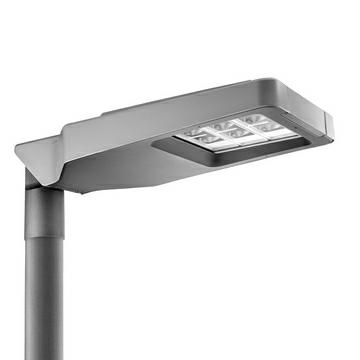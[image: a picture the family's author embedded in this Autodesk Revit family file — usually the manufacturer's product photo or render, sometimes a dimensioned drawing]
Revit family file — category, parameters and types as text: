
# Revit family: Lighting-StreetLighting-GEWISS-ROAD[5]MINI-LED_OPTIC_WIDE_CLI
name_source: partatom
category: Apparecchi per illuminazione
units: mm (PartAtom-declared; Revit-internal decimal feet)

## family parameters
Basato su piano di lavoro = No
Condiviso = No
Punto di calcolo locali = No
Quota connettore circolare = Usa diametro
Sempre verticale = Sì
Sorgente d'illuminazione = No
Taglio con vuoti quando caricato = No
Tipo di parte = Normale

## types (28) — shared parameters
Applicazione = External
Carico apparente = 53 VA
Catalogue = LIGHTING
Commenti sul wattaggio = 53W
IDF = 85536a03-eff7-45b7-82af-033095416c36
IDT = 022a80ee4c80461ea9288278e8deede6
IP degree = IP66
Immagine tipo = GWR5276M.jpg
Insulation class = I
Produttore = GEWISS S.p.A.
SEO = Street lighting
Shock resistance = IK08
Technical sheet = https://www.gewiss.com
URL = https://www.gewiss.com
Version file RFA = 20.11
Warranty = 5 years

## per-type parameters (varying)
- GWR5772 - ROAD 5 MINI S.AL.2M 4000K 700mA O.W CL.I: Catalogue Range=ROAD [5]; Colour temperature=4000 K (CRI 70); Colour temperature:=4000 K (CRI 70); Descrizione=ROAD 5 MINI S.AL.2M 4000K 700mA O.W CL.I; EAN code=8011564873339; Electrocod=244C; LED LifeTime (L80B05)=77000H; LED current.=0,7A; Lamp-=LED; Lumen output (lm)=5240; Maximum surface exposed to the wind=0,15M2; Minimum distance from the illuminated object=1M; Modello=GWR5772; No. Chorus modules=2 (2x3 LED); Nominal flux (lm)=6240; Number of modules=2 (2x3 LED); Operating temperature:=-25 +50 °C; Optic=W - ULOR: 0%; Overvoltage resistance=12 KV (Common and dfferential mode); Pilot current=0,7A; System power=53W; Tilt adjustable=-20° ÷ +10° side bracket - -10° ÷ +20° pole head; Tipo alimentatore=Constant Current Driver Led; Tipologia=Stand alone; Type of lamp=LED; Voltage-=220/240 V - 50/60 Hz - Stand alone; Weight (kg)=6,6; Weight (kg):=6,6; Working temperature=-25 +50 °C
- GWR5771B30K - ROAD5 MINI WIDE 1M 3000K 0,7A CL1 BIREG: Body=Die-cast aluminium -; Catalogue Range=ROAD [5]; Classification:=-; Color Rendering Index=CRI-70; Colore=Graphite grey; Colour :=Powder coating; Colour temperature=3000K; Colour temperature:=3000 K (CRI>80); Context=Street and parking lighting; Control System=Bi-power with self-learning; DIN 18032-3 certification=-; Descrizione=GWR5771B30K - ROAD5 MINI WIDE 1M 3000K 0,7A CL1 BIREG; Device with reduced surface temperature=-; Driver=Included; Driver Box=Built-in; Efficiency (lm/W)=100; Electrocod=244C; Eletrical and lighting features=-; External screw=Stainless steel; Fixing=Pole Head - Outreach; Gasket=Anti-aging silicone; General information=-; Glow Wire Test :=-; IPEA=ROAD = A ++ // LARGE AREAS = A3 + // CYCLOPEDONALS = A ++ // GREEN AREAS = A ++ // HISTORICAL CENTER = A5 +; Installationa and maintenance=-; LED Life Time (L80B05)=77000H; LED Maintenance=Not available; LED current.=0,7A; Lamp-=LED; Lifetime=L90B10 (Tq+25°C) = 100.000 h - L90B10 (Tq+50°C) = 75.000 h; Locking Hook=Integrated front handle; Lumen output (lm)=2800; Luminaire=LED Road Equipment; Materials=-; Maximum surface exposed to the wind=0,149999999999999M2; Maximum surface exposed to the wind :=0.15 m²; Minimum distance from the illuminated object=1M; Modello=GWR5771B30K; Mouting and installation=Pole Head - Outreach; Nominal flux (lm)=2700; Number of modules=1 (1x3 LED); Operating temperature :=-25 +50 °C; Operating temperature:=-25 +50 °C; Optic=WIDE; Optic :=Metallized polycarbonate reflector; Optic Maintenance=Not available; Optic and illuminating features=-; Overvoltage protection=DM 10KV / CM 10KV; Overvoltage resistance :=Common and dfferential mode: 10KV; Photobiological Risk Class=RG0; Power supply operation=Bi power; Rated frequency (Hz)=50 / 60; Shield type=4mm thick flat tempered glass; Standard Deviation Colour Matching=SDCM = 5; Standard-=EN 60598-2-3, EN 60598-1 IEC/TR 62778; Standards and approvals=-; Stocking temperature=-; Supply voltage=220 - 240 V; System power=28W; System power :=28 W @ 0.7A; Tilt adjustable=-20° ÷ +10° side bracket - -10° ÷ +20° pole head; Tilt-=-20° ÷ +10° side bracket - -10° ÷ +20° pole head; Tipo alimentatore=Constant Current Driver Led; Tipologia=Bi power; Type of light source=LED - Not replaceable; Unified Glare Rating=G*3 - ULOR = 0; Unique digital code (Datamatrix)=Currently not present; Voltage-=220/240 V - 50/60 Hz - Bi-power with self-learning; Weight (kg):=6,4; Wiring=Isolating switch
- GWR571230K - ROAD5 MINI WIDE 2M 3000K 1,0A CL1: Body=Die-cast aluminium -; Catalogue Range=ROAD [5]; Classification:=-; Color Rendering Index=CRI-70; Colore=Graphite grey; Colour :=Powder coating; Colour temperature=3000K; Colour temperature:=3000 K (CRI>80); Context=Street and parking lighting; Control System=Stand alone; DIN 18032-3 certification=-; Descrizione=GWR571230K - ROAD5 MINI WIDE 2M 3000K 1,0A CL1; Device with reduced surface temperature=-; Driver=Included; Driver Box=Built-in; Efficiency (lm/W)=101; Electrocod=244C; Eletrical and lighting features=-; External screw=Stainless steel; Fixing=Pole Head - Outreach; Gasket=Anti-aging silicone; General information=-; Glow Wire Test :=-; IPEA=ROAD = A ++ // LARGE AREAS = A3 + // CYCLOPEDONALS = A + // GREEN AREAS = A + // HISTORICAL CENTER = A5 +; Installationa and maintenance=-; LED Life Time (L80B05)=120000H; LED Maintenance=Not available; LED current.=0,9A; Lamp-=LED; Lifetime=L90B10 (Tq+25°C) = 100.000 h - L90B10 (Tq+40°C) = 75.000 h; Locking Hook=Integrated front handle; Lumen output (lm)=6800; Luminaire=LED Road Equipment; Materials=-; Maximum surface exposed to the wind=0,149999999999999M2; Maximum surface exposed to the wind :=0.15 m²; Minimum distance from the illuminated object=1M; Modello=GWR571230K; Mouting and installation=Pole Head - Outreach; Nominal flux (lm)=8280; Number of modules=2 (2x3 LED); Operating temperature :=-25 +40 °C; Operating temperature:=-25 +40 °C; Optic=WIDE; Optic :=Metallized polycarbonate reflector; Optic Maintenance=Not available; Optic and illuminating features=-; Overvoltage protection=DM 10KV / CM 10KV; Overvoltage resistance :=Common and dfferential mode: 10KV; Photobiological Risk Class=RG0; Rated frequency (Hz)=50 / 60; Shield type=4mm thick flat tempered glass; Standard Deviation Colour Matching=SDCM = 5; Standard-=EN 60598-2-3, EN 60598-1 IEC/TR 62778; Standards and approvals=-; Stocking temperature=-; Supply voltage=220 - 240 V; System power=76W; System power :=67 W @ 0.9A; Tilt adjustable=-20° ÷ +10° side bracket - -10° ÷ +20° pole head; Tilt-=-20° ÷ +10° side bracket - -10° ÷ +20° pole head; Tipo alimentatore=Constant Current Driver Led; Tipologia=Stand alone; Type of light source=LED - Not replaceable; Unified Glare Rating=G*3 - ULOR = 0; Unique digital code (Datamatrix)=Currently not present; Voltage-=220/240 V - 50/60 Hz - Stand alone; Weight (kg):=6,6; Wiring=Isolating switch
- GWR571130K - ROAD5 MINI WIDE 1M 3000K 1,0A CL1: Body=Die-cast aluminium -; Catalogue Range=ROAD [5]; Classification:=-; Color Rendering Index=CRI-70; Colore=Graphite grey; Colour :=Powder coating; Colour temperature=3000K; Colour temperature:=3000 K (CRI>80); Context=Street and parking lighting; Control System=Stand alone; DIN 18032-3 certification=-; Descrizione=GWR571130K - ROAD5 MINI WIDE 1M 3000K 1,0A CL1; Device with reduced surface temperature=-; Driver=Included; Driver Box=Built-in; Efficiency (lm/W)=97; Electrocod=244C; Eletrical and lighting features=-; External screw=Stainless steel; Fixing=Pole Head - Outreach; Gasket=Anti-aging silicone; General information=-; Glow Wire Test :=-; IPEA=ROAD = A ++ // LARGE AREAS = A ++ // CYCLOPEDONALS = A + // GREEN AREAS = A + // HISTORICAL CENTER = A5 +; Installationa and maintenance=-; LED Life Time (L80B05)=120000H; LED Maintenance=Not available; LED current.=1A; Lamp-=LED; Lifetime=L90B10 (Tq+25°C) = 100.000 h - L90B10 (Tq+40°C) = 75.000 h; Locking Hook=Integrated front handle; Lumen output (lm)=3700; Luminaire=LED Road Equipment; Materials=-; Maximum surface exposed to the wind=0,149999999999999M2; Maximum surface exposed to the wind :=0.15 m²; Minimum distance from the illuminated object=1M; Modello=GWR571130K; Mouting and installation=Pole Head - Outreach; Nominal flux (lm)=4140; Number of modules=1 (1x3 LED); Operating temperature :=-25 +40 °C; Operating temperature:=-25 +40 °C; Optic=WIDE; Optic :=Metallized polycarbonate reflector; Optic Maintenance=Not available; Optic and illuminating features=-; Overvoltage protection=DM 10KV / CM 10KV; Overvoltage resistance :=Common and dfferential mode: 10KV; Photobiological Risk Class=RG0; Rated frequency (Hz)=50 / 60; Shield type=4mm thick flat tempered glass; Standard Deviation Colour Matching=SDCM = 5; Standard-=EN 60598-2-3, EN 60598-1 IEC/TR 62778; Standards and approvals=-; Stocking temperature=-; Supply voltage=220 - 240 V; System power=38W; System power :=38 W @ 1A; Tilt adjustable=-20° ÷ +10° side bracket - -10° ÷ +20° pole head; Tilt-=-20° ÷ +10° side bracket - -10° ÷ +20° pole head; Tipo alimentatore=Constant Current Driver Led; Tipologia=Stand alone; Type of light source=LED - Not replaceable; Unified Glare Rating=G*3 - ULOR = 0; Unique digital code (Datamatrix)=Currently not present; Voltage-=220/240 V - 50/60 Hz - Stand alone; Weight (kg):=6,4; Wiring=Isolating switch
- GWR5772M30K - ROAD5 MINI WIDE 2M 3000K 0,7A CL1 1-10V: Body=Die-cast aluminium -; Catalogue Range=ROAD [5]; Classification:=-; Color Rendering Index=CRI-70; Colore=Graphite grey; Colour :=Powder coating; Colour temperature=3000K; Colour temperature:=3000 K (CRI>80); Context=Street and parking lighting; Control System=Dimmable 1-10 V; DIN 18032-3 certification=-; Descrizione=GWR5772M30K - ROAD5 MINI WIDE 2M 3000K 0,7A CL1 1-10V; Device with reduced surface temperature=-; Driver=Included; Driver Box=Built-in; Efficiency (lm/W)=102; Electrocod=244C; Eletrical and lighting features=-; External screw=Stainless steel; Fixing=Pole Head - Outreach; Gasket=Anti-aging silicone; General information=-; Glow Wire Test :=-; IPEA=ROAD = A ++ // LARGE AREAS = A3 + // CYCLOPEDONALS = A ++ // GREEN AREAS = A ++ // HISTORICAL CENTER = A5 +; Installationa and maintenance=-; LED Life Time (L80B05)=77000H; LED Maintenance=Not available; LED current.=0,7A; Lamp-=LED; Lifetime=L90B10 (Tq+25°C) = 100.000 h - L90B10 (Tq+50°C) = 75.000 h; Locking Hook=Integrated front handle; Lumen output (lm)=5500; Luminaire=LED Road Equipment; Materials=-; Maximum surface exposed to the wind=0,149999999999999M2; Maximum surface exposed to the wind :=0.15 m²; Minimum distance from the illuminated object=1M; Modello=GWR5772M30K; Mouting and installation=Pole Head - Outreach; Nominal flux (lm)=5400; Number of modules=2 (2x3 LED); Operating temperature :=-25 +50 °C; Operating temperature:=-25 +50 °C; Optic=WIDE; Optic :=Metallized polycarbonate reflector; Optic Maintenance=Not available; Optic and illuminating features=-; Overvoltage protection=DM 10KV / CM 10KV; Overvoltage resistance :=Common and dfferential mode: 10KV; Photobiological Risk Class=RG0; Power supply operation=Dimmable; Rated frequency (Hz)=50 / 60; Shield type=4mm thick flat tempered glass; Standard Deviation Colour Matching=SDCM = 5; Standard-=EN 60598-2-3, EN 60598-1 IEC/TR 62778; Standards and approvals=-; Stocking temperature=-; Supply voltage=220 - 240 V; System power=53W; System power :=54 W @ 0.7A; Tilt adjustable=-20° ÷ +10° side bracket - -10° ÷ +20° pole head; Tilt-=-20° ÷ +10° side bracket - -10° ÷ +20° pole head; Tipo alimentatore=Constant Current Driver Led; Tipologia=Dimmable; Type of light source=LED - Not replaceable; Unified Glare Rating=G*3 - ULOR = 0; Unique digital code (Datamatrix)=Currently not present; Voltage-=220/240 V - 50/60 Hz - Dimmable 1-10 V; Weight (kg):=6,6; Wiring=Isolating switch
- GWR5712B - ROAD5 MINI WIDE 2M 4000K 1,0A CL1 BIREG: Catalogue Range=ROAD [5]; Colour temperature=4000 K (CRI 70); Colour temperature:=4000 K (CRI 70); Descrizione=ROAD 5 MINI BI-POW.2M 4000K 1A O.W CL.I; EAN code=8011564873056; Electrocod=244C; LED LifeTime (L80B05)=120000H; LED current.=1A; Lamp-=LED; Lumen output (lm)=7680; Maximum surface exposed to the wind=0,15M2; Minimum distance from the illuminated object=1M; Modello=GWR5712B; No. Chorus modules=2 (2x3 LED); Nominal flux (lm)=9540; Number of modules=2 (2x3 LED); Operating temperature:=-25 +40 °C; Optic=W - ULOR: 0%; Overvoltage resistance=12 KV (Common and dfferential mode); Pilot current=1A; Power supply operation=Bi power; System power=77W; Tilt adjustable=-20° ÷ +10° side bracket - -10° ÷ +20° pole head; Tipo alimentatore=Constant Current Driver Led; Tipologia=Bi power; Type of lamp=LED; Voltage-=220/240 V - 50/60 Hz - Bi-power with self-learning; Weight (kg)=6,6; Weight (kg):=6,6; Working temperature=-25 +40 °C
- GWR5712 - ROAD 5 MINI S.AL.2M 4000K 1A O.W CL.I: Catalogue Range=ROAD [5]; Colour temperature=4000 K (CRI 70); Colour temperature:=4000 K (CRI 70); Descrizione=ROAD 5 MINI S.AL.2M 4000K 1A O.W CL.I; EAN code=8011564873049; Electrocod=244C; LED LifeTime (L80B05)=120000H; LED current.=1A; Lamp-=LED; Lumen output (lm)=7680; Maximum surface exposed to the wind=0,15M2; Minimum distance from the illuminated object=1M; Modello=GWR5712; No. Chorus modules=2 (2x3 LED); Nominal flux (lm)=9540; Number of modules=2 (2x3 LED); Operating temperature:=-25 +40 °C; Optic=W - ULOR: 0%; Overvoltage resistance=12 KV (Common and dfferential mode); Pilot current=1A; System power=76W; Tilt adjustable=-20° ÷ +10° side bracket - -10° ÷ +20° pole head; Tipo alimentatore=Constant Current Driver Led; Tipologia=Stand alone; Type of lamp=LED; Voltage-=220/240 V - 50/60 Hz - Stand alone; Weight (kg)=6,6; Weight (kg):=6,6; Working temperature=-25 +40 °C
- GWR5711 - ROAD 5 MINI S.AL.1M 4000K 1A O.W CL.I: Catalogue Range=ROAD [5]; Colour temperature=4000 K (CRI 70); Colour temperature:=4000 K (CRI 70); Descrizione=ROAD 5 MINI S.AL.1M 4000K 1A O.W CL.I; EAN code=8011564873018; Electrocod=244C; LED LifeTime (L80B05)=120000H; LED current.=1A; Lamp-=LED; Lumen output (lm)=3840; Maximum surface exposed to the wind=0,15M2; Minimum distance from the illuminated object=1M; Modello=GWR5711; No. Chorus modules=1 (1x3 LED); Nominal flux (lm)=4770; Number of modules=1 (1x3 LED); Operating temperature:=-25 +40 °C; Optic=W - ULOR: 0%; Overvoltage resistance=12 KV (Common and dfferential mode); Pilot current=1A; System power=38W; Tilt adjustable=-20° ÷ +10° side bracket - -10° ÷ +20° pole head; Tipo alimentatore=Constant Current Driver Led; Tipologia=Stand alone; Type of lamp=LED; Voltage-=220/240 V - 50/60 Hz - Stand alone; Weight (kg)=6,4; Weight (kg):=6,4; Working temperature=-25 +40 °C
- GWR5711V - ROAD5 MINI V.WIDE 1M 4000K 1,0A CL1: Body=Die-cast aluminium -; Classification:=-; Color Rendering Index=CRI-70; Colore=Graphite grey; Colour :=Powder coating; Colour temperature=4000K; Context=Street and parking lighting; Control System=DALI; DIN 18032-3 certification=-; Descrizione=GWR5711V - ROAD5 MINI V.WIDE 1M 4000K 1,0A CL1; Device with reduced surface temperature=-; Driver=Included; Driver Box=Built-in; Efficiency (lm/W)=110; Eletrical and lighting features=-; External screw=Stainless steel; Fixing=Pole Head - Outreach; Gasket=Anti-aging silicone; General information=-; Glow Wire Test :=-; IPEA=ROAD = A4 + // LARGE AREAS = A4 + // CYCLOPEDONALS = A3 + // GREEN AREAS = A3 + // HISTORICAL CENTER = A6 +; Installationa and maintenance=-; LED Maintenance=Not available; Lifetime=L90B10 (Tq+25°C) = 100.000 h - L90B10 (Tq+40°C) = 75.000 h; Locking Hook=Integrated front handle; Lumen output (lm)=4300; Luminaire=LED Road Equipment; Materials=-; Maximum surface exposed to the wind :=0.15 m²; Modello=GWR5711V; Mouting and installation=Pole Head - Outreach; Number of modules=1 (1x3 LED); Operating temperature :=-25 +40 °C; Optic=WIDE; Optic :=Metallized polycarbonate reflector; Optic Maintenance=Not available; Optic and illuminating features=-; Overvoltage protection=DM 10KV / CM 10KV; Photobiological Risk Class=RG0; Rated frequency (Hz)=50 / 60; Shield type=4mm thick flat tempered glass; Standard Deviation Colour Matching=SDCM = 5; Standard-=EN 60598-2-3, EN 60598-1 IEC/TR 62778; Standards and approvals=-; Stocking temperature=-; Supply voltage=220 - 240 V; System power :=39 W @ 1A; Tilt-=-20° ÷ +10° side bracket - -10° ÷ +20° pole head; Type of light source=LED - Not replaceable; Unified Glare Rating=G*3 - ULOR = 0; Unique digital code (Datamatrix)=Currently not present; Weight (kg):=6,4; Wiring=Isolating switch
- GWR5772B30K - ROAD5 MINI WIDE 2M 3000K 0,7A CL1 BIREG: Body=Die-cast aluminium -; Catalogue Range=ROAD [5]; Classification:=-; Color Rendering Index=CRI-70; Colore=Graphite grey; Colour :=Powder coating; Colour temperature=3000K; Colour temperature:=3000 K (CRI>80); Context=Street and parking lighting; Control System=Bi-power with self-learning; DIN 18032-3 certification=-; Descrizione=GWR5772B30K - ROAD5 MINI WIDE 2M 3000K 0,7A CL1 BIREG; Device with reduced surface temperature=-; Driver=Included; Driver Box=Built-in; Efficiency (lm/W)=102; Electrocod=244C; Eletrical and lighting features=-; External screw=Stainless steel; Fixing=Pole Head - Outreach; Gasket=Anti-aging silicone; General information=-; Glow Wire Test :=-; IPEA=ROAD = A ++ // LARGE AREAS = A3 + // CYCLOPEDONALS = A ++ // GREEN AREAS = A ++ // HISTORICAL CENTER = A5 +; Installationa and maintenance=-; LED Life Time (L80B05)=77000H; LED Maintenance=Not available; LED current.=0,7A; Lamp-=LED; Lifetime=L90B10 (Tq+25°C) = 100.000 h - L90B10 (Tq+50°C) = 75.000 h; Locking Hook=Integrated front handle; Lumen output (lm)=5500; Luminaire=LED Road Equipment; Materials=-; Maximum surface exposed to the wind=0,149999999999999M2; Maximum surface exposed to the wind :=0.15 m²; Minimum distance from the illuminated object=1M; Modello=GWR5772B30K; Mouting and installation=Pole Head - Outreach; Nominal flux (lm)=5400; Number of modules=2 (2x3 LED); Operating temperature :=-25 +50 °C; Operating temperature:=-25 +50 °C; Optic=WIDE; Optic :=Metallized polycarbonate reflector; Optic Maintenance=Not available; Optic and illuminating features=-; Overvoltage protection=DM 10KV / CM 10KV; Overvoltage resistance :=Common and dfferential mode: 10KV; Photobiological Risk Class=RG0; Power supply operation=Bi power; Rated frequency (Hz)=50 / 60; Shield type=4mm thick flat tempered glass; Standard Deviation Colour Matching=SDCM = 5; Standard-=EN 60598-2-3, EN 60598-1 IEC/TR 62778; Standards and approvals=-; Stocking temperature=-; Supply voltage=220 - 240 V; System power=54W; System power :=54 W @ 0.7A; Tilt adjustable=-20° ÷ +10° side bracket - -10° ÷ +20° pole head; Tilt-=-20° ÷ +10° side bracket - -10° ÷ +20° pole head; Tipo alimentatore=Constant Current Driver Led; Tipologia=Bi power; Type of light source=LED - Not replaceable; Unified Glare Rating=G*3 - ULOR = 0; Unique digital code (Datamatrix)=Currently not present; Voltage-=220/240 V - 50/60 Hz - Bi-power with self-learning; Weight (kg):=6,6; Wiring=Isolating switch
- GWR577130K - ROAD5 MINI WIDE 1M 3000K 0,7A CL1: Body=Die-cast aluminium -; Catalogue Range=ROAD [5]; Classification:=-; Color Rendering Index=CRI-70; Colore=Graphite grey; Colour :=Powder coating; Colour temperature=3000K; Colour temperature:=3000 K (CRI>80); Context=Street and parking lighting; Control System=Stand alone; DIN 18032-3 certification=-; Descrizione=GWR577130K - ROAD5 MINI WIDE 1M 3000K 0,7A CL1; Device with reduced surface temperature=-; Driver=Included; Driver Box=Built-in; Efficiency (lm/W)=104; Electrocod=244C; Eletrical and lighting features=-; External screw=Stainless steel; Fixing=Pole Head - Outreach; Gasket=Anti-aging silicone; General information=-; Glow Wire Test :=-; IPEA=ROAD = A3 + // LARGE AREAS = A3 + // CYCLOPEDONALS = A ++ // GREEN AREAS = A ++ // HISTORICAL CENTER = A6 +; Installationa and maintenance=-; LED Life Time (L80B05)=77000H; LED Maintenance=Not available; LED current.=0,7A; Lamp-=LED; Lifetime=L90B10 (Tq+25°C) = 100.000 h - L90B10 (Tq+50°C) = 75.000 h; Locking Hook=Integrated front handle; Lumen output (lm)=2800; Luminaire=LED Road Equipment; Materials=-; Maximum surface exposed to the wind=0,149999999999999M2; Maximum surface exposed to the wind :=0.15 m²; Minimum distance from the illuminated object=1M; Modello=GWR577130K; Mouting and installation=Pole Head - Outreach; Nominal flux (lm)=2700; Number of modules=1 (1x3 LED); Operating temperature :=-25 +50 °C; Operating temperature:=-25 +50 °C; Optic=WIDE; Optic :=Metallized polycarbonate reflector; Optic Maintenance=Not available; Optic and illuminating features=-; Overvoltage protection=DM 10KV / CM 10KV; Overvoltage resistance :=Common and dfferential mode: 10KV; Photobiological Risk Class=RG0; Rated frequency (Hz)=50 / 60; Shield type=4mm thick flat tempered glass; Standard Deviation Colour Matching=SDCM = 5; Standard-=EN 60598-2-3, EN 60598-1 IEC/TR 62778; Standards and approvals=-; Stocking temperature=-; Supply voltage=220 - 240 V; System power=27W; System power :=27 W @ 0.7A; Tilt adjustable=-20° ÷ +10° side bracket - -10° ÷ +20° pole head; Tilt-=-20° ÷ +10° side bracket - -10° ÷ +20° pole head; Tipo alimentatore=Constant Current Driver Led; Tipologia=Stand alone; Type of light source=LED - Not replaceable; Unified Glare Rating=G*3 - ULOR = 0; Unique digital code (Datamatrix)=Currently not present; Voltage-=220/240 V - 50/60 Hz - Stand alone; Weight (kg):=6,4; Wiring=Isolating switch
- GWR5711B - ROAD5 MINI WIDE 1M 4000K 1,0A CL1 BIREG: Catalogue Range=ROAD [5]; Colour temperature=4000 K (CRI 70); Colour temperature:=4000 K (CRI 70); Descrizione=ROAD 5 MINI BI-POW.1M 4000K 1A O.W CL.I; EAN code=8011564873025; Electrocod=244C; LED LifeTime (L80B05)=120000H; LED current.=1A; Lamp-=LED; Lumen output (lm)=3840; Maximum surface exposed to the wind=0,15M2; Minimum distance from the illuminated object=1M; Modello=GWR5711B; No. Chorus modules=1 (1x3 LED); Nominal flux (lm)=4770; Number of modules=1 (1x3 LED); Operating temperature:=-25 +40 °C; Optic=W - ULOR: 0%; Overvoltage resistance=12 KV (Common and dfferential mode); Pilot current=1A; Power supply operation=Bi power; System power=39W; Tilt adjustable=-20° ÷ +10° side bracket - -10° ÷ +20° pole head; Tipo alimentatore=Constant Current Driver Led; Tipologia=Bi power; Type of lamp=LED; Voltage-=220/240 V - 50/60 Hz - Bi-power with self-learning; Weight (kg)=6,4; Weight (kg):=6,4; Working temperature=-25 +40 °C
- GWR5731 - ROAD5 MINI WIDE 1M 4000K 0,35A CL1: Catalogue Range=ROAD [5]; Colour temperature=4000 K (CRI 70); Colour temperature:=4000 K (CRI 70); Descrizione=ROAD 5 MINI S.AL.1M 4000K 350mA O.W CL.I; EAN code=8011564873193; Electrocod=244C; LED LifeTime (L80B05)=77000H; LED current.=0,35A; Lamp-=LED; Lumen output (lm)=1310; Maximum surface exposed to the wind=0,15M2; Minimum distance from the illuminated object=1M; Modello=GWR5731; No. Chorus modules=1 (1x3 LED); Nominal flux (lm)=1560; Number of modules=1 (1x3 LED); Operating temperature:=-25 +50 °C; Optic=W - ULOR: 0%; Overvoltage resistance=12 KV (Common and dfferential mode); Pilot current=0,35A; System power=14W; Tilt adjustable=-20° ÷ +10° side bracket - -10° ÷ +20° pole head; Tipo alimentatore=Constant Current Driver Led; Tipologia=Stand alone; Type of lamp=LED; Voltage-=220/240 V - 50/60 Hz - Stand alone; Weight (kg)=6,4; Weight (kg):=6,4; Working temperature=-25 +50 °C
- GWR5771M30K - ROAD5 MINI WIDE 1M 3000K 0,7A CL1 1-10V: Body=Die-cast aluminium -; Catalogue Range=ROAD [5]; Classification:=-; Color Rendering Index=CRI-70; Colore=Graphite grey; Colour :=Powder coating; Colour temperature=3000K; Colour temperature:=3000 K (CRI>80); Context=Street and parking lighting; Control System=Dimmable 1-10 V; DIN 18032-3 certification=-; Descrizione=GWR5771M30K - ROAD5 MINI WIDE 1M 3000K 0,7A CL1 1-10V; Device with reduced surface temperature=-; Driver=Included; Driver Box=Built-in; Efficiency (lm/W)=100; Electrocod=244C; Eletrical and lighting features=-; External screw=Stainless steel; Fixing=Pole Head - Outreach; Gasket=Anti-aging silicone; General information=-; Glow Wire Test :=-; IPEA=ROAD = A ++ // LARGE AREAS = A3 + // CYCLOPEDONALS = A ++ // GREEN AREAS = A ++ // HISTORICAL CENTER = A5 +; Installationa and maintenance=-; LED Life Time (L80B05)=77000H; LED Maintenance=Not available; LED current.=0,7A; Lamp-=LED; Lifetime=L90B10 (Tq+25°C) = 100.000 h - L90B10 (Tq+50°C) = 75.000 h; Locking Hook=Integrated front handle; Lumen output (lm)=2800; Luminaire=LED Road Equipment; Materials=-; Maximum surface exposed to the wind=0,149999999999999M2; Maximum surface exposed to the wind :=0.15 m²; Minimum distance from the illuminated object=1M; Modello=GWR5771M30K; Mouting and installation=Pole Head - Outreach; Nominal flux (lm)=2700; Number of modules=1 (1x3 LED); Operating temperature :=-25 +50 °C; Operating temperature:=-25 +50 °C; Optic=WIDE; Optic :=Metallized polycarbonate reflector; Optic Maintenance=Not available; Optic and illuminating features=-; Overvoltage protection=DM 10KV / CM 10KV; Overvoltage resistance :=Common and dfferential mode: 10KV; Photobiological Risk Class=RG0; Power supply operation=Dimmable; Rated frequency (Hz)=50 / 60; Shield type=4mm thick flat tempered glass; Standard Deviation Colour Matching=SDCM = 5; Standard-=EN 60598-2-3, EN 60598-1 IEC/TR 62778; Standards and approvals=-; Stocking temperature=-; Supply voltage=220 - 240 V; System power=27W; System power :=28 W @ 0.7A; Tilt adjustable=-20° ÷ +10° side bracket - -10° ÷ +20° pole head; Tilt-=-20° ÷ +10° side bracket - -10° ÷ +20° pole head; Tipo alimentatore=Constant Current Driver Led; Tipologia=Dimmable; Type of light source=LED - Not replaceable; Unified Glare Rating=G*3 - ULOR = 0; Unique digital code (Datamatrix)=Currently not present; Voltage-=220/240 V - 50/60 Hz - Dimmable 1-10 V; Weight (kg):=6,4; Wiring=Isolating switch
- GWR5711M - ROAD5 MINI WIDE 1M 4000K 1,0A CL1 1-10V: Catalogue Range=ROAD [5]; Colour temperature=4000 K (CRI 70); Colour temperature:=4000 K (CRI 70); Descrizione=ROAD 5 MINI DIM.1M 4000K 1A O.W CL.I; EAN code=8011564873032; Electrocod=244C; LED LifeTime (L80B05)=120000H; LED current.=1A; Lamp-=LED; Lumen output (lm)=3840; Maximum surface exposed to the wind=0,15M2; Minimum distance from the illuminated object=1M; Modello=GWR5711M; No. Chorus modules=1 (1x3 LED); Nominal flux (lm)=4770; Number of modules=1 (1x3 LED); Operating temperature:=-25 +40 °C; Optic=W - ULOR: 0%; Overvoltage resistance=12 KV (Common and dfferential mode); Pilot current=1A; Power supply operation=Dimmable; System power=38W; Tilt adjustable=-20° ÷ +10° side bracket - -10° ÷ +20° pole head; Tipo alimentatore=Constant Current Driver Led; Tipologia=Dimmable; Type of lamp=LED; Voltage-=220/240 V - 50/60 Hz - Dimmable 1-10 V; Weight (kg)=6,4; Weight (kg):=6,4; Working temperature=-25 +40 °C
- GWR5712M - ROAD5 MINI WIDE 2M 4000K 1,0A CL1 1-10V: Catalogue Range=ROAD [5]; Colour temperature=4000 K (CRI 70); Colour temperature:=4000 K (CRI 70); Descrizione=ROAD 5 MINI DIM.2M 4000K 1A O.W CL.I; EAN code=8011564873063; Electrocod=244C; LED LifeTime (L80B05)=120000H; LED current.=1A; Lamp-=LED; Lumen output (lm)=7680; Maximum surface exposed to the wind=0,15M2; Minimum distance from the illuminated object=1M; Modello=GWR5712M; No. Chorus modules=2 (2x3 LED); Nominal flux (lm)=9540; Number of modules=2 (2x3 LED); Operating temperature:=-25 +40 °C; Optic=W - ULOR: 0%; Overvoltage resistance=12 KV (Common and dfferential mode); Pilot current=1A; Power supply operation=Dimmable; System power=76W; Tilt adjustable=-20° ÷ +10° side bracket - -10° ÷ +20° pole head; Tipo alimentatore=Constant Current Driver Led; Tipologia=Dimmable; Type of lamp=LED; Voltage-=220/240 V - 50/60 Hz - Dimmable 1-10 V; Weight (kg)=6,6; Weight (kg):=6,6; Working temperature=-25 +40 °C
- GWR5712M30K - ROAD5 MINI WIDE 2M 3000K 1,0A CL1 1-10V: Body=Die-cast aluminium -; Catalogue Range=ROAD [5]; Classification:=-; Color Rendering Index=CRI-70; Colore=Graphite grey; Colour :=Powder coating; Colour temperature=3000K; Colour temperature:=3000 K (CRI>80); Context=Street and parking lighting; Control System=Dimmable 1-10 V; DIN 18032-3 certification=-; Descrizione=GWR5712M30K - ROAD5 MINI WIDE 2M 3000K 1,0A CL1 1-10V; Device with reduced surface temperature=-; Driver=Included; Driver Box=Built-in; Efficiency (lm/W)=96; Electrocod=244C; Eletrical and lighting features=-; External screw=Stainless steel; Fixing=Pole Head - Outreach; Gasket=Anti-aging silicone; General information=-; Glow Wire Test :=-; IPEA=ROAD = A + // LARGE AREAS = A ++ // CYCLOPEDONALS = A + // GREEN AREAS = A + // HISTORICAL CENTER = A5 +; Installationa and maintenance=-; LED Life Time (L80B05)=120000H; LED Maintenance=Not available; LED current.=1A; Lamp-=LED; Lifetime=L90B10 (Tq+25°C) = 100.000 h - L90B10 (Tq+40°C) = 75.000 h; Locking Hook=Integrated front handle; Lumen output (lm)=7400; Luminaire=LED Road Equipment; Materials=-; Maximum surface exposed to the wind=0,149999999999999M2; Maximum surface exposed to the wind :=0.15 m²; Minimum distance from the illuminated object=1M; Modello=GWR5712M30K; Mouting and installation=Pole Head - Outreach; Nominal flux (lm)=8280; Number of modules=2 (2x3 LED); Operating temperature :=-25 +40 °C; Operating temperature:=-25 +40 °C; Optic=WIDE; Optic :=Metallized polycarbonate reflector; Optic Maintenance=Not available; Optic and illuminating features=-; Overvoltage protection=DM 10KV / CM 10KV; Overvoltage resistance :=Common and dfferential mode: 10KV; Photobiological Risk Class=RG0; Power supply operation=Dimmable; Rated frequency (Hz)=50 / 60; Shield type=4mm thick flat tempered glass; Standard Deviation Colour Matching=SDCM = 5; Standard-=EN 60598-2-3, EN 60598-1 IEC/TR 62778; Standards and approvals=-; Stocking temperature=-; Supply voltage=220 - 240 V; System power=76W; System power :=77 W @ 1A; Tilt adjustable=-20° ÷ +10° side bracket - -10° ÷ +20° pole head; Tilt-=-20° ÷ +10° side bracket - -10° ÷ +20° pole head; Tipo alimentatore=Constant Current Driver Led; Tipologia=Dimmable; Type of light source=LED - Not replaceable; Unified Glare Rating=G*3 - ULOR = 0; Unique digital code (Datamatrix)=Currently not present; Voltage-=220/240 V - 50/60 Hz - Dimmable 1-10 V; Weight (kg):=6,6; Wiring=Isolating switch
- GWR5772M - ROAD5 MINI WIDE 2M 4000K 0,7A CL1 1-10V: Catalogue Range=ROAD [5]; Colour temperature=4000 K (CRI 70); Colour temperature:=4000 K (CRI 70); Descrizione=ROAD 5 MINI DIM.2M 4000K 700mA O.W CL.I; EAN code=8011564873353; Electrocod=244C; LED LifeTime (L80B05)=77000H; LED current.=0,7A; Lamp-=LED; Lumen output (lm)=5240; Maximum surface exposed to the wind=0,15M2; Minimum distance from the illuminated object=1M; Modello=GWR5772M; No. Chorus modules=2 (2x3 LED); Nominal flux (lm)=6240; Number of modules=2 (2x3 LED); Operating temperature:=-25 +50 °C; Optic=W - ULOR: 0%; Overvoltage resistance=12 KV (Common and dfferential mode); Pilot current=0,7A; Power supply operation=Dimmable; System power=53W; Tilt adjustable=-20° ÷ +10° side bracket - -10° ÷ +20° pole head; Tipo alimentatore=Constant Current Driver Led; Tipologia=Dimmable; Type of lamp=LED; Voltage-=220/240 V - 50/60 Hz - Dimmable 1-10 V; Weight (kg)=6,6; Weight (kg):=6,6; Working temperature=-25 +50 °C
- GWR5711B30K - ROAD5 MINI WIDE 1M 3000K 1,0A CL1 BIREG: Body=Die-cast aluminium -; Catalogue Range=ROAD [5]; Classification:=-; Color Rendering Index=CRI-70; Colore=Graphite grey; Colour :=Powder coating; Colour temperature=3000K; Colour temperature:=3000 K (CRI>80); Context=Street and parking lighting; Control System=Bi-power with self-learning; DIN 18032-3 certification=-; Descrizione=GWR5711B30K - ROAD5 MINI WIDE 1M 3000K 1,0A CL1 BIREG; Device with reduced surface temperature=-; Driver=Included; Driver Box=Built-in; Efficiency (lm/W)=95; Electrocod=244C; Eletrical and lighting features=-; External screw=Stainless steel; Fixing=Pole Head - Outreach; Gasket=Anti-aging silicone; General information=-; Glow Wire Test :=-; IPEA=ROAD = A + // LARGE AREAS = A ++ // CYCLOPEDONALS = A + // GREEN AREAS = A + // HISTORICAL CENTER = A4 +; Installationa and maintenance=-; LED Life Time (L80B05)=120000H; LED Maintenance=Not available; LED current.=1A; Lamp-=LED; Lifetime=L90B10 (Tq+25°C) = 100.000 h - L90B10 (Tq+40°C) = 75.000 h; Locking Hook=Integrated front handle; Lumen output (lm)=3700; Luminaire=LED Road Equipment; Materials=-; Maximum surface exposed to the wind=0,149999999999999M2; Maximum surface exposed to the wind :=0.15 m²; Minimum distance from the illuminated object=1M; Modello=GWR5711B30K; Mouting and installation=Pole Head - Outreach; Nominal flux (lm)=4140; Number of modules=1 (1x3 LED); Operating temperature :=-25 +40 °C; Operating temperature:=-25 +40 °C; Optic=WIDE; Optic :=Metallized polycarbonate reflector; Optic Maintenance=Not available; Optic and illuminating features=-; Overvoltage protection=DM 10KV / CM 10KV; Overvoltage resistance :=Common and dfferential mode: 10KV; Photobiological Risk Class=RG0; Power supply operation=Bi power; Rated frequency (Hz)=50 / 60; Shield type=4mm thick flat tempered glass; Standard Deviation Colour Matching=SDCM = 5; Standard-=EN 60598-2-3, EN 60598-1 IEC/TR 62778; Standards and approvals=-; Stocking temperature=-; Supply voltage=220 - 240 V; System power=39W; System power :=39 W @ 1A; Tilt adjustable=-20° ÷ +10° side bracket - -10° ÷ +20° pole head; Tilt-=-20° ÷ +10° side bracket - -10° ÷ +20° pole head; Tipo alimentatore=Constant Current Driver Led; Tipologia=Bi power; Type of light source=LED - Not replaceable; Unified Glare Rating=G*3 - ULOR = 0; Unique digital code (Datamatrix)=Currently not present; Voltage-=220/240 V - 50/60 Hz - Bi-power with self-learning; Weight (kg):=6,4; Wiring=Isolating switch
- GWR5712V - ROAD5 MINI V.WIDE 2M 4000K 1,0A CL1: Body=Die-cast aluminium -; Classification:=-; Color Rendering Index=CRI-70; Colore=Graphite grey; Colour :=Powder coating; Colour temperature=4000K; Context=Street and parking lighting; Control System=DALI; DIN 18032-3 certification=-; Descrizione=GWR5712V - ROAD5 MINI V.WIDE 2M 4000K 1,0A CL1; Device with reduced surface temperature=-; Driver=Included; Driver Box=Built-in; Efficiency (lm/W)=110; Eletrical and lighting features=-; External screw=Stainless steel; Fixing=Pole Head - Outreach; Gasket=Anti-aging silicone; General information=-; Glow Wire Test :=-; IPEA=ROAD = A3 + // LARGE AREAS = A4 + // CYCLOPEDONALS = A ++ // GREEN AREAS = A ++ // HISTORICAL CENTER = A6 +; Installationa and maintenance=-; LED Maintenance=Not available; Lifetime=L90B10 (Tq+25°C) = 100.000 h - L90B10 (Tq+40°C) = 75.000 h; Locking Hook=Integrated front handle; Lumen output (lm)=8500; Luminaire=LED Road Equipment; Materials=-; Maximum surface exposed to the wind :=0.15 m²; Modello=GWR5712V; Mouting and installation=Pole Head - Outreach; Number of modules=2 (2x3 LED); Operating temperature :=-25 +40 °C; Optic=WIDE; Optic :=Metallized polycarbonate reflector; Optic Maintenance=Not available; Optic and illuminating features=-; Overvoltage protection=DM 10KV / CM 10KV; Photobiological Risk Class=RG0; Rated frequency (Hz)=50 / 60; Shield type=4mm thick flat tempered glass; Standard Deviation Colour Matching=SDCM = 5; Standard-=EN 60598-2-3, EN 60598-1 IEC/TR 62778; Standards and approvals=-; Stocking temperature=-; Supply voltage=220 - 240 V; System power :=77 W @ 1A; Tilt-=-20° ÷ +10° side bracket - -10° ÷ +20° pole head; Type of light source=LED - Not replaceable; Unified Glare Rating=G*3 - ULOR = 0; Unique digital code (Datamatrix)=Currently not present; Weight (kg):=6,59999999999999; Wiring=Isolating switch
- GWR573130K - ROAD5 MINI WIDE 1M 3000K 0,35A CL1: Body=Die-cast aluminium -; Catalogue Range=ROAD [5]; Classification:=-; Color Rendering Index=CRI-70; Colore=Graphite grey; Colour :=Powder coating; Colour temperature=3000K; Colour temperature:=3000 K (CRI>80); Context=Street and parking lighting; Control System=Stand alone; DIN 18032-3 certification=-; Descrizione=GWR573130K - ROAD5 MINI WIDE 1M 3000K 0,35A CL1; Device with reduced surface temperature=-; Driver=Included; Driver Box=Built-in; Efficiency (lm/W)=115; Electrocod=244C; Eletrical and lighting features=-; External screw=Stainless steel; Fixing=Pole Head - Outreach; Gasket=Anti-aging silicone; General information=-; Glow Wire Test :=-; IPEA=ROAD = A4 + // LARGE AREAS = A5 + // CYCLOPEDONALS = A4 + // GREEN AREAS = A4 + // HISTORICAL CENTER = A6 +; Installationa and maintenance=-; LED Life Time (L80B05)=77000H; LED Maintenance=Not available; LED current.=0,35A; Lamp-=LED; Lifetime=L90B10 (Tq+25°C) = 100.000 h - L90B10 (Tq+50°C) = 75.000 h; Locking Hook=Integrated front handle; Lumen output (lm)=1500; Luminaire=LED Road Equipment; Materials=-; Maximum surface exposed to the wind=0,149999999999999M2; Maximum surface exposed to the wind :=0.15 m²; Minimum distance from the illuminated object=1M; Modello=GWR573130K; Mouting and installation=Pole Head - Outreach; Nominal flux (lm)=1350; Number of modules=1 (1x3 LED); Operating temperature :=-25 +50 °C; Operating temperature:=-25 +50 °C; Optic=WIDE; Optic :=Metallized polycarbonate reflector; Optic Maintenance=Not available; Optic and illuminating features=-; Overvoltage protection=DM 10KV / CM 10KV; Overvoltage resistance :=Common and dfferential mode: 10KV; Photobiological Risk Class=RG0; Rated frequency (Hz)=50 / 60; Shield type=4mm thick flat tempered glass; Standard Deviation Colour Matching=SDCM = 5; Standard-=EN 60598-2-3, EN 60598-1 IEC/TR 62778; Standards and approvals=-; Stocking temperature=-; Supply voltage=220 - 240 V; System power=14W; System power :=13 W @ 0.35A; Tilt adjustable=-20° ÷ +10° side bracket - -10° ÷ +20° pole head; Tilt-=-20° ÷ +10° side bracket - -10° ÷ +20° pole head; Tipo alimentatore=Constant Current Driver Led; Tipologia=Stand alone; Type of light source=LED - Not replaceable; Unified Glare Rating=G*3 - ULOR = 0; Unique digital code (Datamatrix)=Currently not present; Voltage-=220/240 V - 50/60 Hz - Stand alone; Weight (kg):=6,4; Wiring=Isolating switch
- GWR5771M - ROAD5 MINI WIDE 1M 4000K 0,7A CL1 1-10V: Catalogue Range=ROAD [5]; Colour temperature=4000 K (CRI 70); Colour temperature:=4000 K (CRI 70); Descrizione=ROAD 5 MINI DIM.1M 4000K 700mA O.W CL.I; EAN code=8011564873322; Electrocod=244C; LED LifeTime (L80B05)=77000H; LED current.=0,7A; Lamp-=LED; Lumen output (lm)=2620; Maximum surface exposed to the wind=0,15M2; Minimum distance from the illuminated object=1M; Modello=GWR5771M; No. Chorus modules=1 (1x3 LED); Nominal flux (lm)=3120; Number of modules=1 (1x3 LED); Operating temperature:=-25 +50 °C; Optic=W - ULOR: 0%; Overvoltage resistance=12 KV (Common and dfferential mode); Pilot current=0,7A; Power supply operation=Dimmable; System power=27W; Tilt adjustable=-20° ÷ +10° side bracket - -10° ÷ +20° pole head; Tipo alimentatore=Constant Current Driver Led; Tipologia=Dimmable; Type of lamp=LED; Voltage-=220/240 V - 50/60 Hz - Dimmable 1-10 V; Weight (kg)=6,4; Weight (kg):=6,4; Working temperature=-25 +50 °C
- GWR5712B30K - ROAD5 MINI WIDE 2M 3000K 1,0A CL1 BIREG: Body=Die-cast aluminium -; Catalogue Range=ROAD [5]; Classification:=-; Color Rendering Index=CRI-70; Colore=Graphite grey; Colour :=Powder coating; Colour temperature=3000K; Colour temperature:=3000 K (CRI>80); Context=Street and parking lighting; Control System=Bi-power with self-learning; DIN 18032-3 certification=-; Descrizione=GWR5712B30K - ROAD5 MINI WIDE 2M 3000K 1,0A CL1 BIREG; Device with reduced surface temperature=-; Driver=Included; Driver Box=Built-in; Efficiency (lm/W)=96; Electrocod=244C; Eletrical and lighting features=-; External screw=Stainless steel; Fixing=Pole Head - Outreach; Gasket=Anti-aging silicone; General information=-; Glow Wire Test :=-; IPEA=ROAD = A + // LARGE AREAS = A ++ // CYCLOPEDONALS = A + // GREEN AREAS = A + // HISTORICAL CENTER = A5 +; Installationa and maintenance=-; LED Life Time (L80B05)=120000H; LED Maintenance=Not available; LED current.=1A; Lamp-=LED; Lifetime=L90B10 (Tq+25°C) = 100.000 h - L90B10 (Tq+40°C) = 75.000 h; Locking Hook=Integrated front handle; Lumen output (lm)=7400; Luminaire=LED Road Equipment; Materials=-; Maximum surface exposed to the wind=0,149999999999999M2; Maximum surface exposed to the wind :=0.15 m²; Minimum distance from the illuminated object=1M; Modello=GWR5712B30K; Mouting and installation=Pole Head - Outreach; Nominal flux (lm)=8280; Number of modules=2 (2x3 LED); Operating temperature :=-25 +40 °C; Operating temperature:=-25 +40 °C; Optic=WIDE; Optic :=Metallized polycarbonate reflector; Optic Maintenance=Not available; Optic and illuminating features=-; Overvoltage protection=DM 10KV / CM 10KV; Overvoltage resistance :=Common and dfferential mode: 10KV; Photobiological Risk Class=RG0; Power supply operation=Bi power; Rated frequency (Hz)=50 / 60; Shield type=4mm thick flat tempered glass; Standard Deviation Colour Matching=SDCM = 5; Standard-=EN 60598-2-3, EN 60598-1 IEC/TR 62778; Standards and approvals=-; Stocking temperature=-; Supply voltage=220 - 240 V; System power=77W; System power :=77 W @ 1A; Tilt adjustable=-20° ÷ +10° side bracket - -10° ÷ +20° pole head; Tilt-=-20° ÷ +10° side bracket - -10° ÷ +20° pole head; Tipo alimentatore=Constant Current Driver Led; Tipologia=Bi power; Type of light source=LED - Not replaceable; Unified Glare Rating=G*3 - ULOR = 0; Unique digital code (Datamatrix)=Currently not present; Voltage-=220/240 V - 50/60 Hz - Bi-power with self-learning; Weight (kg):=6,6; Wiring=Isolating switch
- GWR5772B - ROAD5 MINI WIDE 2M 4000K 0,7A CL1 BIREG: Catalogue Range=ROAD [5]; Colour temperature=4000 K (CRI 70); Colour temperature:=4000 K (CRI 70); Descrizione=ROAD 5 MINI BI-PO.2M4000K 700mA O.W CL.I; EAN code=8011564873346; Electrocod=244C; LED LifeTime (L80B05)=77000H; LED current.=0,7A; Lamp-=LED; Lumen output (lm)=5240; Maximum surface exposed to the wind=0,15M2; Minimum distance from the illuminated object=1M; Modello=GWR5772B; No. Chorus modules=2 (2x3 LED); Nominal flux (lm)=6240; Number of modules=2 (2x3 LED); Operating temperature:=-25 +50 °C; Optic=W - ULOR: 0%; Overvoltage resistance=12 KV (Common and dfferential mode); Pilot current=0,7A; Power supply operation=Bi power; System power=54W; Tilt adjustable=-20° ÷ +10° side bracket - -10° ÷ +20° pole head; Tipo alimentatore=Constant Current Driver Led; Tipologia=Bi power; Type of lamp=LED; Voltage-=220/240 V - 50/60 Hz - Bi-power with self-learning; Weight (kg)=6,6; Weight (kg):=6,6; Working temperature=-25 +50 °C
- GWR577230K - ROAD5 MINI WIDE 2M 3000K 0,7A CL1: Body=Die-cast aluminium -; Catalogue Range=ROAD [5]; Classification:=-; Color Rendering Index=CRI-70; Colore=Graphite grey; Colour :=Powder coating; Colour temperature=3000K; Colour temperature:=3000 K (CRI>80); Context=Street and parking lighting; Control System=Stand alone; DIN 18032-3 certification=-; Descrizione=GWR577230K - ROAD5 MINI WIDE 2M 3000K 0,7A CL1; Device with reduced surface temperature=-; Driver=Included; Driver Box=Built-in; Efficiency (lm/W)=104; Electrocod=244C; Eletrical and lighting features=-; External screw=Stainless steel; Fixing=Pole Head - Outreach; Gasket=Anti-aging silicone; General information=-; Glow Wire Test :=-; IPEA=ROAD = A3 + // LARGE AREAS = A3 + // CYCLOPEDONALS = A ++ // GREEN AREAS = A ++ // HISTORICAL CENTER = A6 +; Installationa and maintenance=-; LED Life Time (L80B05)=77000H; LED Maintenance=Not available; LED current.=0,7A; Lamp-=LED; Lifetime=L90B10 (Tq+25°C) = 100.000 h - L90B10 (Tq+50°C) = 75.000 h; Locking Hook=Integrated front handle; Lumen output (lm)=5500; Luminaire=LED Road Equipment; Materials=-; Maximum surface exposed to the wind=0,149999999999999M2; Maximum surface exposed to the wind :=0.15 m²; Minimum distance from the illuminated object=1M; Modello=GWR577230K; Mouting and installation=Pole Head - Outreach; Nominal flux (lm)=5400; Number of modules=2 (2x3 LED); Operating temperature :=-25 +50 °C; Operating temperature:=-25 +50 °C; Optic=WIDE; Optic :=Metallized polycarbonate reflector; Optic Maintenance=Not available; Optic and illuminating features=-; Overvoltage protection=DM 10KV / CM 10KV; Overvoltage resistance :=Common and dfferential mode: 10KV; Photobiological Risk Class=RG0; Rated frequency (Hz)=50 / 60; Shield type=4mm thick flat tempered glass; Standard Deviation Colour Matching=SDCM = 5; Standard-=EN 60598-2-3, EN 60598-1 IEC/TR 62778; Standards and approvals=-; Stocking temperature=-; Supply voltage=220 - 240 V; System power=53W; System power :=53 W @ 0.7A; Tilt adjustable=-20° ÷ +10° side bracket - -10° ÷ +20° pole head; Tilt-=-20° ÷ +10° side bracket - -10° ÷ +20° pole head; Tipo alimentatore=Constant Current Driver Led; Tipologia=Stand alone; Type of light source=LED - Not replaceable; Unified Glare Rating=G*3 - ULOR = 0; Unique digital code (Datamatrix)=Currently not present; Voltage-=220/240 V - 50/60 Hz - Stand alone; Weight (kg):=6,6; Wiring=Isolating switch
- GWR5771B - ROAD5 MINI WIDE 1M 4000K 0,7A CL1 BIREG: Catalogue Range=ROAD [5]; Colour temperature=4000 K (CRI 70); Colour temperature:=4000 K (CRI 70); Descrizione=ROAD 5 MINI BI-PO.1M4000K 700mA O.W CL.I; EAN code=8011564873315; Electrocod=244C; LED LifeTime (L80B05)=77000H; LED current.=0,7A; Lamp-=LED; Lumen output (lm)=2620; Maximum surface exposed to the wind=0,15M2; Minimum distance from the illuminated object=1M; Modello=GWR5771B; No. Chorus modules=1 (1x3 LED); Nominal flux (lm)=3120; Number of modules=1 (1x3 LED); Operating temperature:=-25 +50 °C; Optic=W - ULOR: 0%; Overvoltage resistance=12 KV (Common and dfferential mode); Pilot current=0,7A; Power supply operation=Bi power; System power=28W; Tilt adjustable=-20° ÷ +10° side bracket - -10° ÷ +20° pole head; Tipo alimentatore=Constant Current Driver Led; Tipologia=Bi power; Type of lamp=LED; Voltage-=220/240 V - 50/60 Hz - Bi-power with self-learning; Weight (kg)=6,4; Weight (kg):=6,4; Working temperature=-25 +50 °C
- GWR5711M30K - ROAD5 MINI WIDE 1M 3000K 1,0A CL1 1-10V: Body=Die-cast aluminium -; Catalogue Range=ROAD [5]; Classification:=-; Color Rendering Index=CRI-70; Colore=Graphite grey; Colour :=Powder coating; Colour temperature=3000K; Colour temperature:=3000 K (CRI>80); Context=Street and parking lighting; Control System=Dimmable 1-10 V; DIN 18032-3 certification=-; Descrizione=GWR5711M30K - ROAD5 MINI WIDE 1M 3000K 1,0A CL1 1-10V; Device with reduced surface temperature=-; Driver=Included; Driver Box=Built-in; Efficiency (lm/W)=95; Electrocod=244C; Eletrical and lighting features=-; External screw=Stainless steel; Fixing=Pole Head - Outreach; Gasket=Anti-aging silicone; General information=-; Glow Wire Test :=-; IPEA=ROAD = A + // LARGE AREAS = A ++ // CYCLOPEDONALS = A + // GREEN AREAS = A + // HISTORICAL CENTER = A4 +; Installationa and maintenance=-; LED Life Time (L80B05)=120000H; LED Maintenance=Not available; LED current.=1A; Lamp-=LED; Lifetime=L90B10 (Tq+25°C) = 100.000 h - L90B10 (Tq+40°C) = 75.000 h; Locking Hook=Integrated front handle; Lumen output (lm)=3700; Luminaire=LED Road Equipment; Materials=-; Maximum surface exposed to the wind=0,149999999999999M2; Maximum surface exposed to the wind :=0.15 m²; Minimum distance from the illuminated object=1M; Modello=GWR5711M30K; Mouting and installation=Pole Head - Outreach; Nominal flux (lm)=4140; Number of modules=1 (1x3 LED); Operating temperature :=-25 +40 °C; Operating temperature:=-25 +40 °C; Optic=WIDE; Optic :=Metallized polycarbonate reflector; Optic Maintenance=Not available; Optic and illuminating features=-; Overvoltage protection=DM 10KV / CM 10KV; Overvoltage resistance :=Common and dfferential mode: 10KV; Photobiological Risk Class=RG0; Power supply operation=Dimmable; Rated frequency (Hz)=50 / 60; Shield type=4mm thick flat tempered glass; Standard Deviation Colour Matching=SDCM = 5; Standard-=EN 60598-2-3, EN 60598-1 IEC/TR 62778; Standards and approvals=-; Stocking temperature=-; Supply voltage=220 - 240 V; System power=38W; System power :=39 W @ 1A; Tilt adjustable=-20° ÷ +10° side bracket - -10° ÷ +20° pole head; Tilt-=-20° ÷ +10° side bracket - -10° ÷ +20° pole head; Tipo alimentatore=Constant Current Driver Led; Tipologia=Dimmable; Type of light source=LED - Not replaceable; Unified Glare Rating=G*3 - ULOR = 0; Unique digital code (Datamatrix)=Currently not present; Voltage-=220/240 V - 50/60 Hz - Dimmable 1-10 V; Weight (kg):=6,4; Wiring=Isolating switch
- GWR5771 - ROAD5 MINI WIDE 1M 4000K 0,7A CL1: Catalogue Range=ROAD [5]; Colour temperature=4000 K (CRI 70); Colour temperature:=4000 K (CRI 70); Descrizione=ROAD 5 MINI S.AL.1M 4000K 700mA O.W CL.I; EAN code=8011564873209; Electrocod=244C; LED LifeTime (L80B05)=77000H; LED current.=0,7A; Lamp-=LED; Lumen output (lm)=2620; Maximum surface exposed to the wind=0,15M2; Minimum distance from the illuminated object=1M; Modello=GWR5771; No. Chorus modules=1 (1x3 LED); Nominal flux (lm)=3120; Number of modules=1 (1x3 LED); Operating temperature:=-25 +50 °C; Optic=W - ULOR: 0%; Overvoltage resistance=12 KV (Common and dfferential mode); Pilot current=0,7A; System power=27W; Tilt adjustable=-20° ÷ +10° side bracket - -10° ÷ +20° pole head; Tipo alimentatore=Constant Current Driver Led; Tipologia=Stand alone; Type of lamp=LED; Voltage-=220/240 V - 50/60 Hz - Stand alone; Weight (kg)=6,4; Weight (kg):=6,4; Working temperature=-25 +50 °C
